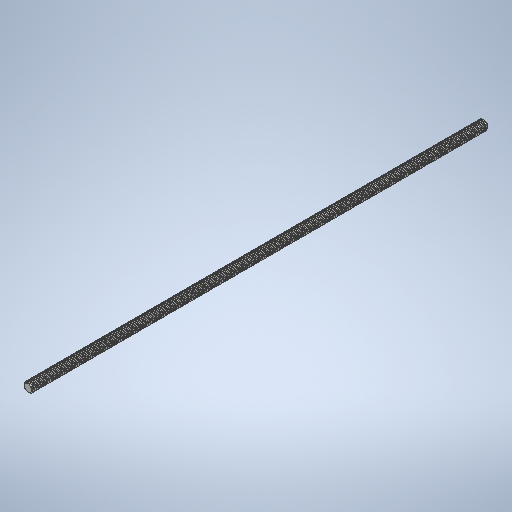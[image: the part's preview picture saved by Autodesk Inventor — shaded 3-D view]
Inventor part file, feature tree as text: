
AUTODESK INVENTOR PART (.ipt)
format: ipt  version: 2025.2 (Build 292293000, 293)  size: 1,657,344 bytes
history: native  units: mm
features: extrude x1, chamfer x1, other x1, pattern_circular x1
ambient origin geometry x8: Origin, YZ Plane, XZ Plane, XY Plane, X Axis, Y Axis, Z Axis, Center Point
bodies: Solid1 (feature_tree)
feature tree (4):
  extrude  "1000mm Rod"  Depth=385.0mm TaperAngle=0.0deg
  chamfer  "Chamfer1"  Distance=0.907143mm Angle=45.0deg
  other  "ACME Thread 2mm Pitch"
  pattern_circular  "4 Start"  [2 undecoded]
note: 2 required parameter values undecoded (feature->parameter linkage not recoverable at this tier; creation-order binding heuristic only, values carry confidence <= 0.55)
